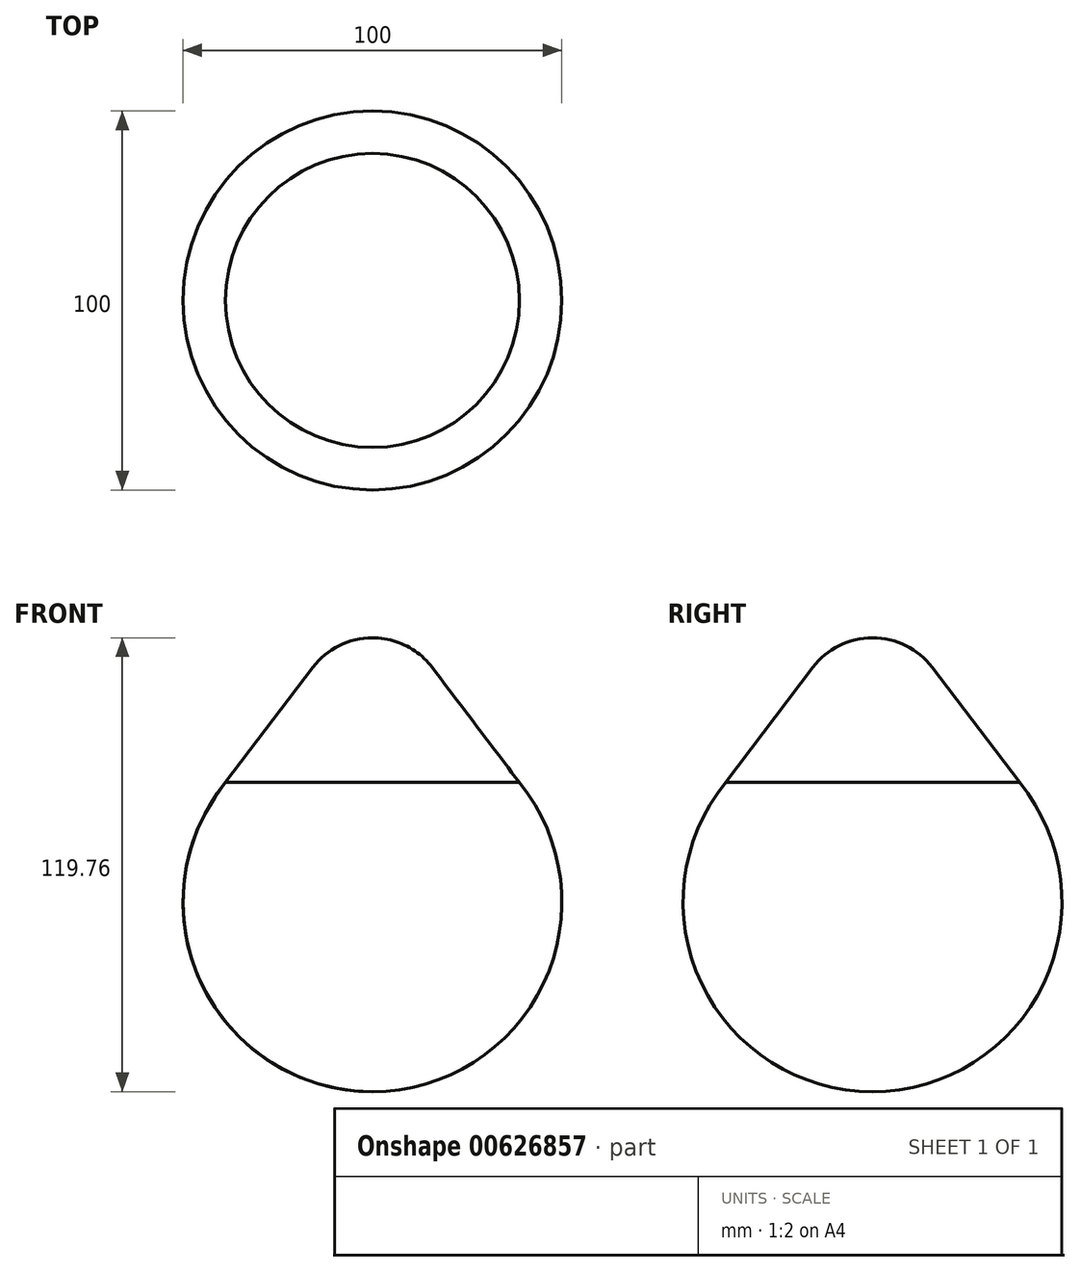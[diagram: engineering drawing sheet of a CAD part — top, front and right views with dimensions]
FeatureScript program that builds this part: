
annotation { "Feature Type Name" : "Feature", "Feature Type Description" : "" }
export const myFeature = defineFeature(function(context is Context, id is Id, definition is map)
    precondition{}
    {
        {
            var Q0;
            Q0=qCreatedBy(makeId("Front.planeOp"),FACE);
            var sketch = newSketch(context, id + "F0", { "sketchPlane" : qUnion([Q0])});
            skArc(sketch, "E0", {"start": v(-38.8, 31.55) * mm, "mid": v(-45.15, -21.48) * mm, "end": v(0, -50) * mm});
            skLineSegment(sketch, "E1", {"start": v(-38.8, 31.55) * mm, "end": v(-15.74, 61.94) * mm});
            skLineSegment(sketch, "E2", {"start": v(0, 69.76) * mm, "end": v(0, -50) * mm});
            skArc(sketch, "E3.trimOffspring", {"start": v(0, 69.76) * mm, "mid": v(-8.79, 67.7) * mm, "end": v(-15.74, 61.94) * mm});
            skSolve(sketch);
        }
        {
            var Q0;
            Q0=makeQuery(id+"F0.imprint","IMPRINT",FACE,{"disambiguationData":[TD([[makeQuery(id+"F0.imprint","IMPRINT",EDGE,{"derivedFrom":sQuery(id+"F0.wireOp",EDGE,"E0")}),1.0]])]});
            var Q1;
            Q1=sQuery(id+"F0.wireOp",EDGE,"E2");
            revolve(context, id + "F1", {"entities" : qUnion([Q0]), "axis" : qUnion([Q1]), "revolveType" : RevolveType.FULL});
        }
    });
